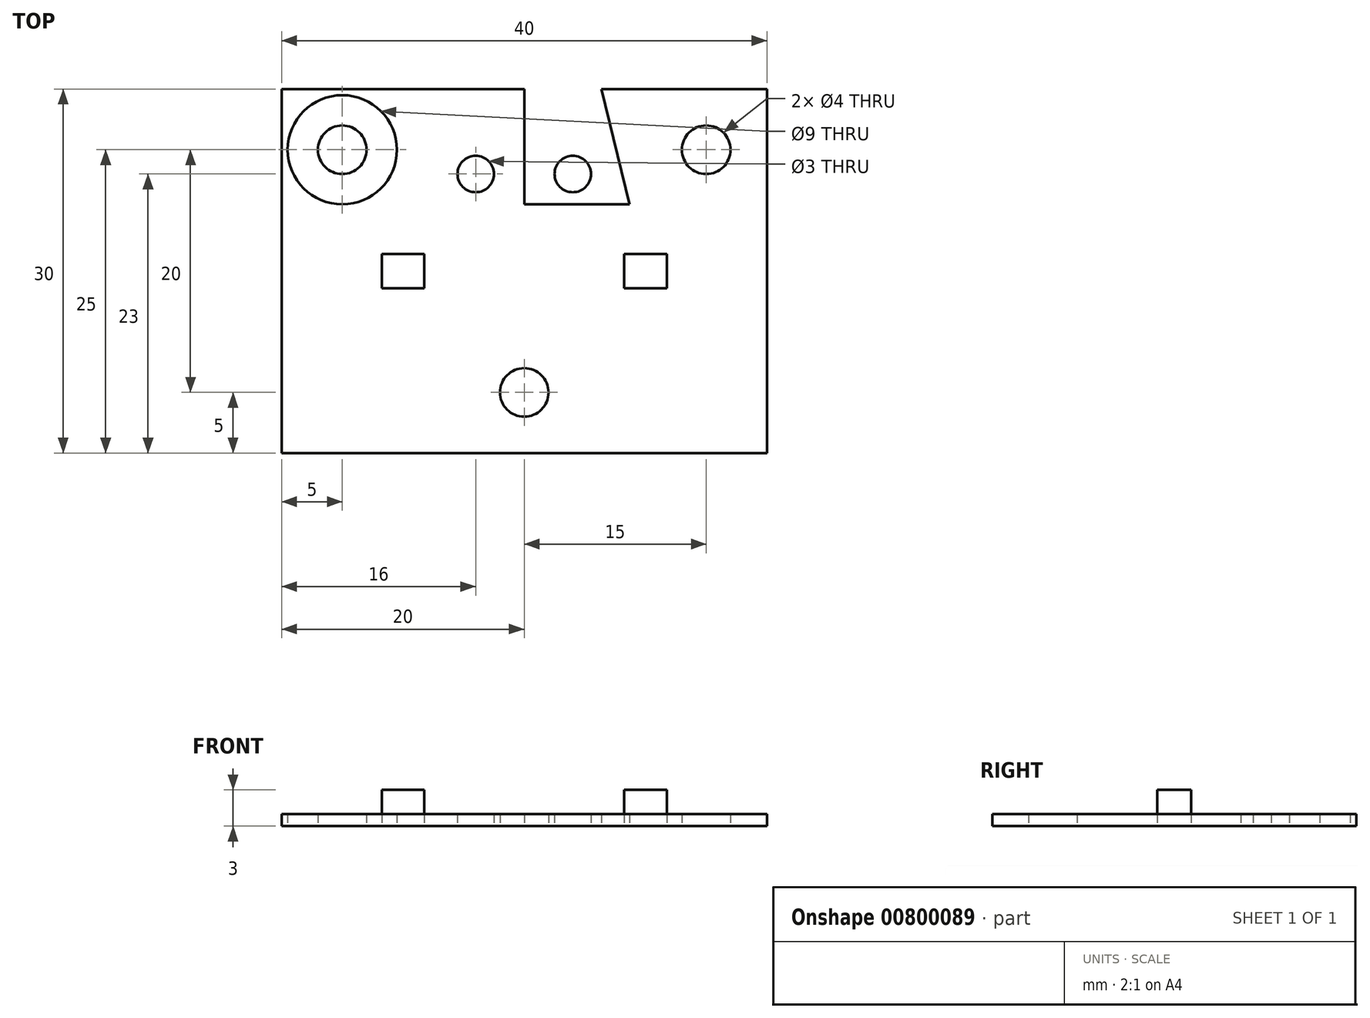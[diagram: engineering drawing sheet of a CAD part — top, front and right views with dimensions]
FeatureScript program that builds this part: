
annotation { "Feature Type Name" : "Feature", "Feature Type Description" : "" }
export const myFeature = defineFeature(function(context is Context, id is Id, definition is map)
    precondition{}
    {
        {
            var Q0;
            Q0=qCreatedBy(makeId("Top.planeOp"),FACE);
            var sketch = newSketch(context, id + "F0", { "sketchPlane" : qUnion([Q0])});
            skLineSegment(sketch, "E0.bottom", {"start": v(0, 0) * mm, "end": v(40, 0) * mm});
            skLineSegment(sketch, "E0.top", {"start": v(0, 30) * mm, "end": v(40, 30) * mm});
            skLineSegment(sketch, "E0.left", {"start": v(0, 0) * mm, "end": v(0, 30) * mm});
            skLineSegment(sketch, "E0.right", {"start": v(40, 0) * mm, "end": v(40, 30) * mm});
            skLineSegment(sketch, "E1", {"start": v(20, 30) * mm, "end": v(20, 0) * mm});
            skCircle(sketch, "E2", {"center": v(16, 23) * mm, "radius": 1.5 * mm});
            skCircle(sketch, "E3.MirrorC", {"center": v(24, 23) * mm, "radius": 1.5 * mm});
            skCircle(sketch, "E4", {"center": v(35, 25) * mm, "radius": 2 * mm});
            skCircle(sketch, "E5", {"center": v(35, 25) * mm, "radius": 4.5 * mm});
            skCircle(sketch, "E6.MirrorC", {"center": v(5, 25) * mm, "radius": 2 * mm});
            skCircle(sketch, "E7.MirrorC", {"center": v(5, 25) * mm, "radius": 4.5 * mm});
            skCircle(sketch, "E8", {"center": v(20, 5) * mm, "radius": 2 * mm});
            skCircle(sketch, "E9", {"center": v(20, 5) * mm, "radius": 4.5 * mm});
            skPoint(sketch, "E10.startSnap0", {"position": v(0, 15) * mm});
            skLineSegment(sketch, "E11", {"start": v(10, 14) * mm, "end": v(10, 16) * mm});
            skLineSegment(sketch, "E12.MirrorCS", {"start": v(30, 14) * mm, "end": v(30, 16) * mm});
            skLineSegment(sketch, "E13", {"start": v(11, 15) * mm, "end": v(10, 15) * mm});
            skLineSegment(sketch, "E14.MirrorCS", {"start": v(29, 15) * mm, "end": v(30, 15) * mm});
            skLineSegment(sketch, "E15.bottom", {"start": v(5, 20.5) * mm, "end": v(35, 20.5) * mm});
            skLineSegment(sketch, "E15.top", {"start": v(5, 9.5) * mm, "end": v(35, 9.5) * mm});
            skLineSegment(sketch, "E15.left", {"start": v(5, 20.5) * mm, "end": v(5, 9.5) * mm});
            skLineSegment(sketch, "E15.right", {"start": v(35, 20.5) * mm, "end": v(35, 9.5) * mm});
            skLineSegment(sketch, "E16.MirrorCS", {"start": v(9, 15) * mm, "end": v(10, 15) * mm});
            skLineSegment(sketch, "E17.MirrorCS", {"start": v(31, 15) * mm, "end": v(30, 15) * mm});
            skText(sketch, "E18", { "text": "CU free", "fontName": "OpenSans-Regular.ttf"});
            skLineSegment(sketch, "E19", {"start": v(39.4, 24.04) * mm, "end": v(45.88, 23.09) * mm});
            skText(sketch, "E20", { "text": "solder pad area", "fontName": "OpenSans-Regular.ttf"});
            skLineSegment(sketch, "E21", {"start": v(35, 9.5) * mm, "end": v(45.2, 9.5) * mm});
            skText(sketch, "E22", { "text": "Holes", "fontName": "OpenSans-Regular.ttf"});
            skLineSegment(sketch, "E23", {"start": v(21.55, 3.73) * mm, "end": v(30.84, -4.01) * mm});
            skText(sketch, "E24", { "text": "LED positions", "fontName": "OpenSans-Regular.ttf"});
            skLineSegment(sketch, "E25", {"start": v(30, 15) * mm, "end": v(24.05, 39.5) * mm});
            skLineSegment(sketch, "E26", {"start": v(24.05, 39.5) * mm, "end": v(10, 15) * mm});
            skText(sketch, "E27", { "text": "on backside", "fontName": "OpenSans-Regular.ttf"});
            skPoint(sketch, "E27.firstSnap0", {"position": v(45.2, 8.33) * mm});
            skText(sketch, "E28", { "text": "on topside", "fontName": "OpenSans-Regular.ttf"});
            skLineSegment(sketch, "E29", {"start": v(24.6, 21.62) * mm, "end": v(30.84, -4.01) * mm});
            skLineSegment(sketch, "E30.bottom", {"start": v(11.75, 16.4) * mm, "end": v(8.25, 16.4) * mm});
            skLineSegment(sketch, "E30.top", {"start": v(11.75, 13.6) * mm, "end": v(8.25, 13.6) * mm});
            skLineSegment(sketch, "E30.left", {"start": v(11.75, 16.4) * mm, "end": v(11.75, 13.6) * mm});
            skLineSegment(sketch, "E30.right", {"start": v(8.25, 16.4) * mm, "end": v(8.25, 13.6) * mm});
            skPoint(sketch, "E30.middle", {"position": v(10, 15) * mm});
            skLineSegment(sketch, "E31.MirrorCS", {"start": v(28.25, 13.6) * mm, "end": v(31.75, 13.6) * mm});
            skLineSegment(sketch, "E32.MirrorCS", {"start": v(28.25, 16.4) * mm, "end": v(28.25, 13.6) * mm});
            skLineSegment(sketch, "E33.MirrorCS", {"start": v(31.75, 16.4) * mm, "end": v(31.75, 13.6) * mm});
            skLineSegment(sketch, "E34.MirrorCS", {"start": v(28.25, 16.4) * mm, "end": v(31.75, 16.4) * mm});
            const initialGuessF0  = {"E18": [0.04588, 0.01793, 1, 0, 0.00515], "E20": [0.0452, 0.00516, 1, 0, 0.00634], "E22": [0.03084, -0.01165, 1, 0, 0.00763], "E24": [0.02405, 0.0395, 1, 0, 0.004], "E27": [0.0452, -0.00136, 1, 0, 0.0049], "E28": [0.04375, 0.0345, 1, 0, 0.005]};
            skSetInitialGuess(sketch, initialGuessF0);
            skSolve(sketch);
        }
        {
            var Q0;
            {var subQ7=sQuery(id+"F0.wireOp",EDGE,"E0.left");Q0=makeQuery(id+"F0.imprint","IMPRINT",FACE,{"disambiguationData":[TD([[makeQuery(id+"F0.imprint","IMPRINT",EDGE,{"derivedFrom":subQ7}),-1.0]])]});}
            var Q1;
            Q1=makeQuery(id+"F0.imprint","IMPRINT",FACE,{"disambiguationData":[TD([[makeQuery(id+"F0.imprint","IMPRINT",EDGE,{"derivedFrom":sQuery(id+"F0.wireOp",EDGE,"E6.MirrorC")}),1.0]])]});
            var Q2;
            {var subQ0=sQuery(id+"F0.wireOp",EDGE,"E9");var subQ1=sQuery(id+"F0.wireOp",EDGE,"E1");var subQ2=makeQuery(id+"F0.imprint","INTERSECT",VERTEX,{"disambiguationData":[OD(0.0)],"derivedFrom":[subQ1,subQ0]});Q2=makeQuery(id+"F0.imprint","IMPRINT",FACE,{"disambiguationData":[TD([[makeQuery(id+"F0.imprint","IMPRINT",EDGE,{"disambiguationData":[TD([[subQ2,-1.0]])],"derivedFrom":subQ1}),-1.0]])]});}
            var Q3;
            {var subQ4=sQuery(id+"F0.wireOp",EDGE,"E0.right");Q3=makeQuery(id+"F0.imprint","IMPRINT",FACE,{"disambiguationData":[TD([[makeQuery(id+"F0.imprint","IMPRINT",EDGE,{"derivedFrom":subQ4}),1.0]])]});}
            var Q4;
            {var subQ0=sQuery(id+"F0.wireOp",EDGE,"E9");var subQ1=sQuery(id+"F0.wireOp",EDGE,"E1");var subQ2=makeQuery(id+"F0.imprint","INTERSECT",VERTEX,{"disambiguationData":[OD(0.0)],"derivedFrom":[subQ1,subQ0]});Q4=makeQuery(id+"F0.imprint","IMPRINT",FACE,{"disambiguationData":[TD([[makeQuery(id+"F0.imprint","IMPRINT",EDGE,{"disambiguationData":[TD([[subQ2,-1.0]])],"derivedFrom":subQ1}),1.0]])]});}
            var Q5;
            {var subQ5=sQuery(id+"F0.wireOp",EDGE,"E15.right");Q5=makeQuery(id+"F0.imprint","IMPRINT",FACE,{"disambiguationData":[TD([[makeQuery(id+"F0.imprint","IMPRINT",EDGE,{"derivedFrom":subQ5}),-1.0]])]});}
            var Q6;
            Q6=makeQuery(id+"F0.imprint","IMPRINT",FACE,{"disambiguationData":[TD([[makeQuery(id+"F0.imprint","IMPRINT",EDGE,{"derivedFrom":sQuery(id+"F0.wireOp",EDGE,"E4")}),-1.0]])]});
            var Q7;
            {var subQ0=sQuery(id+"F0.wireOp",EDGE,"E8");var subQ1=sQuery(id+"F0.wireOp",EDGE,"E1");var subQ5=makeQuery(id+"F0.imprint","INTERSECT",VERTEX,{"disambiguationData":[OD(1.0)],"derivedFrom":[subQ1,subQ0]});Q7=makeQuery(id+"F0.imprint","IMPRINT",FACE,{"disambiguationData":[TD([[makeQuery(id+"F0.imprint","IMPRINT",EDGE,{"disambiguationData":[TD([[subQ5,-1.0]])],"derivedFrom":subQ1}),-1.0]])]});}
            var Q8;
            {var subQ0=sQuery(id+"F0.wireOp",EDGE,"E8");var subQ1=sQuery(id+"F0.wireOp",EDGE,"E1");var subQ5=makeQuery(id+"F0.imprint","INTERSECT",VERTEX,{"disambiguationData":[OD(1.0)],"derivedFrom":[subQ1,subQ0]});Q8=makeQuery(id+"F0.imprint","IMPRINT",FACE,{"disambiguationData":[TD([[makeQuery(id+"F0.imprint","IMPRINT",EDGE,{"disambiguationData":[TD([[subQ5,-1.0]])],"derivedFrom":subQ1}),1.0]])]});}
            var Q9;
            {var subQ3=sQuery(id+"F0.wireOp",EDGE,"E1");var subQ8=sQuery(id+"F0.wireOp",EDGE,"E0.top");var subQ9=makeQuery(id+"F0.imprint","INTERSECT",VERTEX,{"derivedFrom":[subQ8,subQ3]});Q9=makeQuery(id+"F0.imprint","IMPRINT",FACE,{"disambiguationData":[TD([[makeQuery(id+"F0.imprint","IMPRINT",EDGE,{"disambiguationData":[TD([[subQ9,1.0]])],"derivedFrom":subQ8}),-1.0]])]});}
            var Q10;
            Q10=makeQuery(id+"F0.imprint","IMPRINT",FACE,{"disambiguationData":[TD([[makeQuery(id+"F0.imprint","IMPRINT",EDGE,{"derivedFrom":sQuery(id+"F0.wireOp",EDGE,"E3.MirrorC")}),1.0]])]});
            var Q11;
            {var subQ7=sQuery(id+"F0.wireOp",EDGE,"E0.top");var subQ9=sQuery(id+"F0.wireOp",EDGE,"E0.right");var subQ10=makeQuery(id+"F0.imprint","INTERSECT",VERTEX,{"derivedFrom":[subQ7,subQ9]});Q11=makeQuery(id+"F0.imprint","IMPRINT",FACE,{"disambiguationData":[TD([[makeQuery(id+"F0.imprint","IMPRINT",EDGE,{"disambiguationData":[TD([[subQ10,1.0]])],"derivedFrom":subQ7}),-1.0]])]});}
            var Q12;
            {var subQ7=sQuery(id+"F0.wireOp",EDGE,"E0.right");var subQ8=sQuery(id+"F0.wireOp",EDGE,"E0.bottom");var subQ9=makeQuery(id+"F0.imprint","INTERSECT",VERTEX,{"derivedFrom":[subQ8,subQ7]});Q12=makeQuery(id+"F0.imprint","IMPRINT",FACE,{"disambiguationData":[TD([[makeQuery(id+"F0.imprint","IMPRINT",EDGE,{"disambiguationData":[TD([[subQ9,1.0]])],"derivedFrom":subQ8}),1.0]])]});}
            var Q13;
            {var subQ0=sQuery(id+"F0.wireOp",EDGE,"E8");var subQ5=sQuery(id+"F0.wireOp",EDGE,"E23");var subQ6=makeQuery(id+"F0.imprint","INTERSECT",VERTEX,{"derivedFrom":[subQ0,subQ5]});Q13=makeQuery(id+"F0.imprint","IMPRINT",FACE,{"disambiguationData":[TD([[makeQuery(id+"F0.imprint","IMPRINT",EDGE,{"disambiguationData":[TD([[subQ6,-1.0]])],"derivedFrom":subQ0}),-1.0]])]});}
            var Q14;
            {var subQ0=sQuery(id+"F0.wireOp",EDGE,"E15.bottom");var subQ5=sQuery(id+"F0.wireOp",EDGE,"E29");var subQ7=makeQuery(id+"F0.imprint","INTERSECT",VERTEX,{"derivedFrom":[subQ0,subQ5]});Q14=makeQuery(id+"F0.imprint","IMPRINT",FACE,{"disambiguationData":[TD([[makeQuery(id+"F0.imprint","IMPRINT",EDGE,{"disambiguationData":[TD([[subQ7,1.0]])],"derivedFrom":subQ0}),-1.0]])]});}
            var Q15;
            {var subQ0=sQuery(id+"F0.wireOp",EDGE,"E23");var subQ1=sQuery(id+"F0.wireOp",EDGE,"E0.bottom");var subQ2=makeQuery(id+"F0.imprint","INTERSECT",VERTEX,{"derivedFrom":[subQ1,subQ0]});Q15=makeQuery(id+"F0.imprint","IMPRINT",FACE,{"disambiguationData":[TD([[makeQuery(id+"F0.imprint","IMPRINT",EDGE,{"disambiguationData":[TD([[subQ2,-1.0]])],"derivedFrom":subQ1}),1.0]])]});}
            var Q16;
            Q16=makeQuery(id+"F0.imprint","IMPRINT",FACE,{"disambiguationData":[TD([[makeQuery(id+"F0.imprint","IMPRINT",EDGE,{"derivedFrom":sQuery(id+"F0.wireOp",EDGE,"E30.top")}),-1.0]])]});
            var Q17;
            Q17=makeQuery(id+"F0.imprint","IMPRINT",FACE,{"disambiguationData":[TD([[makeQuery(id+"F0.imprint","IMPRINT",EDGE,{"derivedFrom":sQuery(id+"F0.wireOp",EDGE,"E31.MirrorCS")}),1.0]])]});
            var Q18;
            {var subQ0=sQuery(id+"F0.wireOp",EDGE,"E15.left");Q18=makeQuery(id+"F0.imprint","IMPRINT",FACE,{"disambiguationData":[TD([[makeQuery(id+"F0.imprint","IMPRINT",EDGE,{"derivedFrom":subQ0}),1.0]])]});}
            extrude(context, id + "F1", {"entities" : qUnion([Q0, Q1, Q2, Q3, Q4, Q5, Q6, Q7, Q8, Q9, Q10, Q11, Q12, Q13, Q14, Q15, Q16, Q17, Q18]), "depth" : 1 * mm, "offsetDistance" : 25 * mm});
        }
        {
            var Q0;
            Q0=makeQuery(id+"F0.imprint","IMPRINT",FACE,{"disambiguationData":[TD([[makeQuery(id+"F0.imprint","IMPRINT",EDGE,{"derivedFrom":sQuery(id+"F0.wireOp",EDGE,"E31.MirrorCS")}),1.0]])]});
            var Q1;
            Q1=makeQuery(id+"F0.imprint","IMPRINT",FACE,{"disambiguationData":[TD([[makeQuery(id+"F0.imprint","IMPRINT",EDGE,{"derivedFrom":sQuery(id+"F0.wireOp",EDGE,"E30.top")}),-1.0]])]});
            extrude(context, id + "F2", {"entities" : qUnion([Q0, Q1]), "depth" : 3 * mm, "offsetDistance" : 25 * mm});
        }
    });
